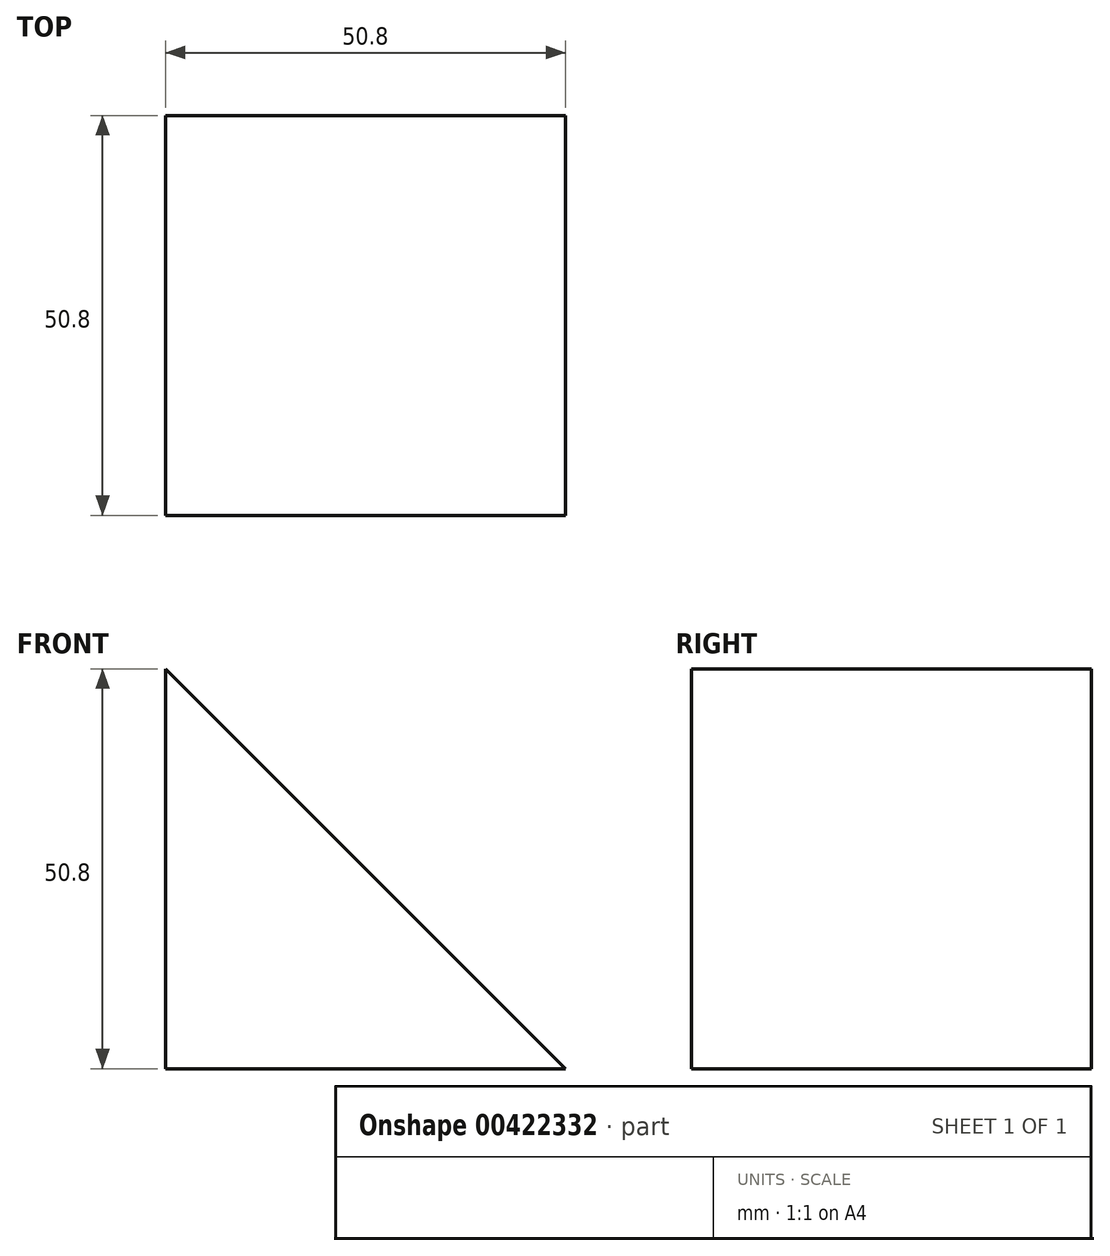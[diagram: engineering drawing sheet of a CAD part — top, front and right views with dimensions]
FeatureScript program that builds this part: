
annotation { "Feature Type Name" : "Feature", "Feature Type Description" : "" }
export const myFeature = defineFeature(function(context is Context, id is Id, definition is map)
    precondition{}
    {
        {
            var Q0;
            Q0=qCreatedBy(makeId("Front.planeOp"),FACE);
            var sketch = newSketch(context, id + "F0", { "sketchPlane" : qUnion([Q0])});
            skLineSegment(sketch, "E0", {"start": v(0, 0) * mm, "end": v(-50.8, 0) * mm});
            skPoint(sketch, "E1.start.orphan", {"position": v(-50.8, 40.62) * mm});
            skLineSegment(sketch, "E2", {"start": v(-50.8, 0) * mm, "end": v(-50.8, 50.8) * mm});
            skLineSegment(sketch, "E3", {"start": v(-50.8, 50.8) * mm, "end": v(0, 0) * mm});
            skSolve(sketch);
        }
        {
            var Q0;
            Q0 = qSketchRegion(id + "F0", true);
            extrude(context, id + "F1", {"entities" : qUnion([Q0]), "depth" : 50.8 * mm});
        }
    });
